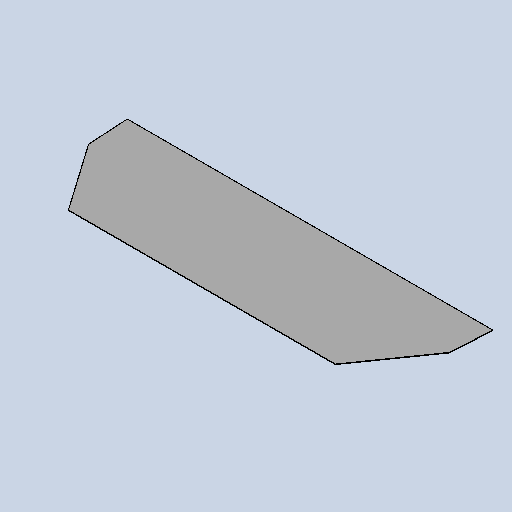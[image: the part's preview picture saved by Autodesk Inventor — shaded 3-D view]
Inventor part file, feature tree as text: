
AUTODESK INVENTOR PART (.ipt)
format: ipt  version: 2025 (Build 290162010, 162A)  size: 275,968 bytes
history: native  units: mm
features: sketch x2, other x2, sheet_metal_op x1, extrude x1, mirror x1, projected_geometry x1
ambient origin geometry x8: Origin, YZ Plane, XZ Plane, XY Plane, X Axis, Y Axis, Z Axis, Center Point
bodies: Solid1 (feature_tree)
feature tree (8):
  sheet_metal_op  "Face1"
  extrude  "Extrusion1"  Depth=450.0mm
  mirror  "Mirror1"
  sketch  "Sketch1"  dims[d0=450.0mm d1=1520.0mm]
  other  "Plate1"
  sketch  "Sketch2"  dims[d2=2.0mm d3=0.1mm d8=10.0mm d9=171.0mm d10=205.0mm d11=0.0mm d12=0.0mm]
  projected_geometry  "Projected Loop1"
  other  "Definition1"
